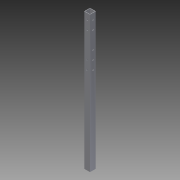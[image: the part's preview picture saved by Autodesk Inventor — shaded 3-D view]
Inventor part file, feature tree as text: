
AUTODESK INVENTOR PART (.ipt)
format: ipt  version: 2013 (Build 170138000, 138)  size: 75,776 bytes
history: native  units: in
note: dims shown in document units (in); Inventor stores cm internally (conversion verified against a paired STEP export)
features: extrude x1, sketch x1
ambient origin geometry x8: Origin, YZ Plane, XZ Plane, XY Plane, X Axis, Y Axis, Z Axis, Center Point
bodies: Solid1 (feature_tree)
feature tree (2):
  extrude  "Extrusion1"  Depth=1.0in
  sketch  "Sketch1"  dims[d0=1.0in d2=1.0in d3=0.0625in d4=23.5in d5=0.0in]
